# Revit family: CENTUM Festpunkt Typ A, Massivanschluss XL100, Gum
name_source: partatom
category: HLS-Bauteile
units: mm (PartAtom-declared; Revit-internal decimal feet)

## family parameters
Arbeitsebenenbasiert = Ja
Beim Laden mit Abzugskörper schneiden = Nein
Bemaßung runder Anschluss = Durchmesser verwenden
Beschriftungsausrichtung beibehalten = Nein
Gemeinsam genutzt = Ja
Immer vertikal = Nein
Klassifizierung = Keine
Raumberechnungspunkt = Nein
Teiletyp = Normal

## types (8) — shared parameters
Anzahl Rohrschellen = 2
Breite Material Rohrschelle = 50 mm
Fabrikat = MEFA
Kurztext1 = Festpunkt Typ A
Länge Druckstück = 116 mm
Material = Stahl
Material Druckstücke = Stahl
Materialname = S235
Materialname Druckstücke = S235JR
Mengeneinheit = St
Oberfläche Druckstücke = blank
Oberfläche Träger + Schellen = galvanisch verzinkt
Rohrschellentyp = Titan HD
Schalldämmeinlage = TPE/EPDM
Stärke Material Rohrschelle = 5 mm
Vorgabe-Ansicht = 1219 mm
max. Axiale Reaktionskraft = 20 kN
max. Temperaturbeständigkeit = 100 °C
vpe = 1
zero-valued in all types: max. Höhe

## per-type parameters (varying)
| type | Artikelnummer | Aufbaumaß | Breite | Breite Profilstahl | EAN | Festpunkt | Gewicht | Gewicht pro Bauteil | Höhe | Höhe Profilstahl | Klammergröße | Kurztext2 | Länge Profilstahl | Profilstahltyp | Rohraußendurchmesser | max. Rohraußendurchmesser | min. Rohraußendurchmesser |
| CENTUM Festpunkt Typ A, Ø60,3 mm m. XL100 Massivanshluss, Gummi | 9993633 | 69 mm | 148 mm  [stored 0.485564 ft] | 65 mm | 4250928454188 | Festpunkt Typ A m.XL100 Massivanschluss Ø60 bis 114_1 : CENTUM Festpunkt Typ A, Ø 60,3, m. XL100 Massivanschluss, Gummi | 6.12 kg | 6.12 kg | 72 mm | 42 mm | 2 | 60,3 mm TPE/EPDM CENTUM<sup>®</sup> Massivanschluss | 200 mm  [stored 0.656168 ft] | U65 | 60 mm  [stored 0.19685 ft] | 0 mm  [stored 0 ft] | 0 mm  [stored 0 ft] |
| CENTUM Festpunkt Typ A, Ø76,1 mm m. XL100 Massivanshluss, Gummi | 9993732 | 69 mm | 166 mm  [stored 0.544619 ft] | 65 mm | 4250928454218 | Festpunkt Typ A m.XL100 Massivanschluss Ø60 bis 114_1 : CENTUM Festpunkt Typ A, Ø 76,1, m. XL100 Massivanschluss, Gummi | 6.36 kg | 6.36 kg | 82 mm | 42 mm | 2 | 76,1 mm TPE/EPDM CENTUM<sup>®</sup> Massivanschluss | 200 mm  [stored 0.656168 ft] | U65 | 76 mm  [stored 0.249344 ft] | 0 mm  [stored 0 ft] | 0 mm  [stored 0 ft] |
| CENTUM Festpunkt Typ A, Ø88,9 mm m. XL100 Massivanshluss, Gummi | 9994027 | 69 mm | 179 mm  [stored 0.58727 ft] | 65 mm | 4250928454232 | Festpunkt Typ A m.XL100 Massivanschluss Ø60 bis 114_1 : CENTUM Festpunkt Typ A, Ø 88,9, m. XL100 Massivanschluss, Gummi | 6.55 kg | 6.55 kg | 90 mm | 42 mm | 2 | 88,9 mm TPE/EPDM CENTUM<sup>®</sup> Massivanschluss | 0 mm  [stored 0 ft] | U65 | 89 mm | 0 mm  [stored 0 ft] | 0 mm  [stored 0 ft] |
| CENTUM Festpunkt Typ A, Ø114,3 mm m. XL100 Massivanshluss, Gummi | 9993256 | 69 mm | 205 mm  [stored 0.672572 ft] | 65 mm | 4250928454195 | Festpunkt Typ A m.XL100 Massivanschluss Ø60 bis 114_1 : CENTUM Festpunkt Typ A, Ø114,3, m. XL100 Massivanschluss, Gummi | 6.93 kg | 6.93 kg | 104 mm | 42 mm | 2 | 114,3 mm TPE/EPDM CENTUM<sup>®</sup> Massivanschluss | 200 mm  [stored 0.656168 ft] | U65 | 114 mm  [stored 0.374016 ft] | 0 mm  [stored 0 ft] | 0 mm  [stored 0 ft] |
| CENTUM Festpunkt Typ A, Ø168,3 mm m. XL100 Massivanshluss, Gummi | 9993734 | 79 mm | 258 mm  [stored 0.846457 ft] | 120 mm | 4250928454225 | CENTUM Festpunkt Typ A m XL100 Massivanschluss, Gummi1 : CENTUM Festpunkt Typ A, Ø 168,3, m. XL100 Massivanschluss, Gummi | 11.75 kg | 11.75 kg | 132 mm | 55 mm |  | 168,3 mm TPE/EPDM CENTUM<sup>®</sup> Massivanschluss | 330 mm  [stored 1.08268 ft] | U120 | 168 mm  [stored 0.551181 ft] | 0 mm  [stored 0 ft] | 0 mm  [stored 0 ft] |
| CENTUM Festpunkt Typ A, Ø219,1 mm m. XL100 Massivanshluss, Gummi | 9992830 | 79 mm | 309 mm  [stored 1.01378 ft] | 120 mm | 4250928454171 | CENTUM Festpunkt Typ A m XL100 Massivanschluss, Gummi1 : CENTUM Festpunkt Typ A, Ø 219,1, m. XL100 Massivanschluss, Gummi | 12.51 kg | 12.51 kg | 161 mm | 55 mm |  | 219,1 mm TPE/EPDM CENTUM<sup>®</sup> Massivanschluss | 330 mm  [stored 1.08268 ft] | U120 | 219 mm  [stored 0.718504 ft] | 0 mm  [stored 0 ft] | 0 mm  [stored 0 ft] |
| CENTUM Festpunkt Typ A, Ø273 mm m. XL100 Massivanshluss, Gummi | 9992178 | 79 mm | 363 mm  [stored 1.19094 ft] | 120 mm | 4250928454164 | CENTUM Festpunkt Typ A m XL100 Massivanschluss, Gummi1 : CENTUM Festpunkt Typ A, Ø 273-274, m. XL100 Massivanschluss, Gummi | 13.32 kg | 13.32 kg | 192 mm | 55 mm |  | 273 - 274 mm TPE/EPDM CENTUM<sup>®</sup> Massivanschluss | 330 mm  [stored 1.08268 ft] | U120 | 0 mm  [stored 0 ft] | 274 mm  [stored 0.89895 ft] | 273 mm  [stored 0.895669 ft] |
| CENTUM Festpunkt Typ A, Ø139,7 mm m. XL100 Massivanshluss, Gummi | 9993733 | 69 mm | 231 mm  [stored 0.757874 ft] | 80 mm | 4250928454201 | Festpunkt Typ A m.XL100 Massivanschluss Ø139,7_1 : CENTUM Festpunkt Typ A, Ø139,7, m. XL100 Massivanschluss, Gummi | 7.69 kg | 7.69 kg | 118 mm | 45 mm | 2 | 139,7 mm TPE/EPDM CENTUM<sup>®</sup> Massivanschluss | 200 mm  [stored 0.656168 ft] | U80 | 140 mm | 0 mm  [stored 0 ft] | 0 mm  [stored 0 ft] |

note: [stored X ft] marks values corroborated as IEEE doubles in the binary element streams (Revit-internal decimal feet)

## geometry (parser evidence)
native form markers: Sweep x25
no freeform markers — native parametric forms only
